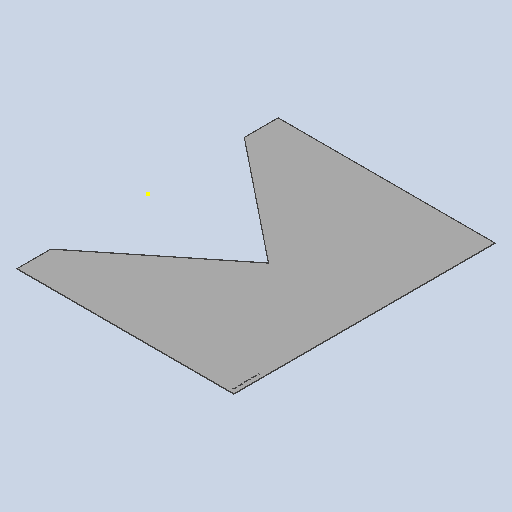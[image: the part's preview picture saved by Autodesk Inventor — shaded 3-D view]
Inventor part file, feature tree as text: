
AUTODESK INVENTOR PART (.ipt)
format: ipt  version: 2025 (Build 290162010, 162A)  size: 204,800 bytes
history: native  units: mm
features: sketch x4, other x4, sheet_metal_op x1, projected_geometry x1
ambient origin geometry x8: Origin, YZ Plane, XZ Plane, XY Plane, X Axis, Y Axis, Z Axis, Center Point
bodies: Solid1 (feature_tree)
feature tree (10):
  sheet_metal_op  "Face1"
  sketch  "Sketch8"  dims[d2=3.0mm]
  other  "Mark1"
  sketch  "Sketch1"  dims[d0=1345.0mm]
  other  "Plate1"
  sketch  "Sketch5"  dims[d1=1620.0mm]
  projected_geometry  "Projected Loop1"
  sketch  "Sketch9"  dims[d26=500.0mm d27=8.37758mm d28=672.816365mm d29=750.0mm d30=1200.0mm d31=3.0mm d32=0.0mm d36=200.0mm d37=15.0mm d38=25.0mm d39=25.0mm]
  other  "Cut1"
  other  "Definition1"
